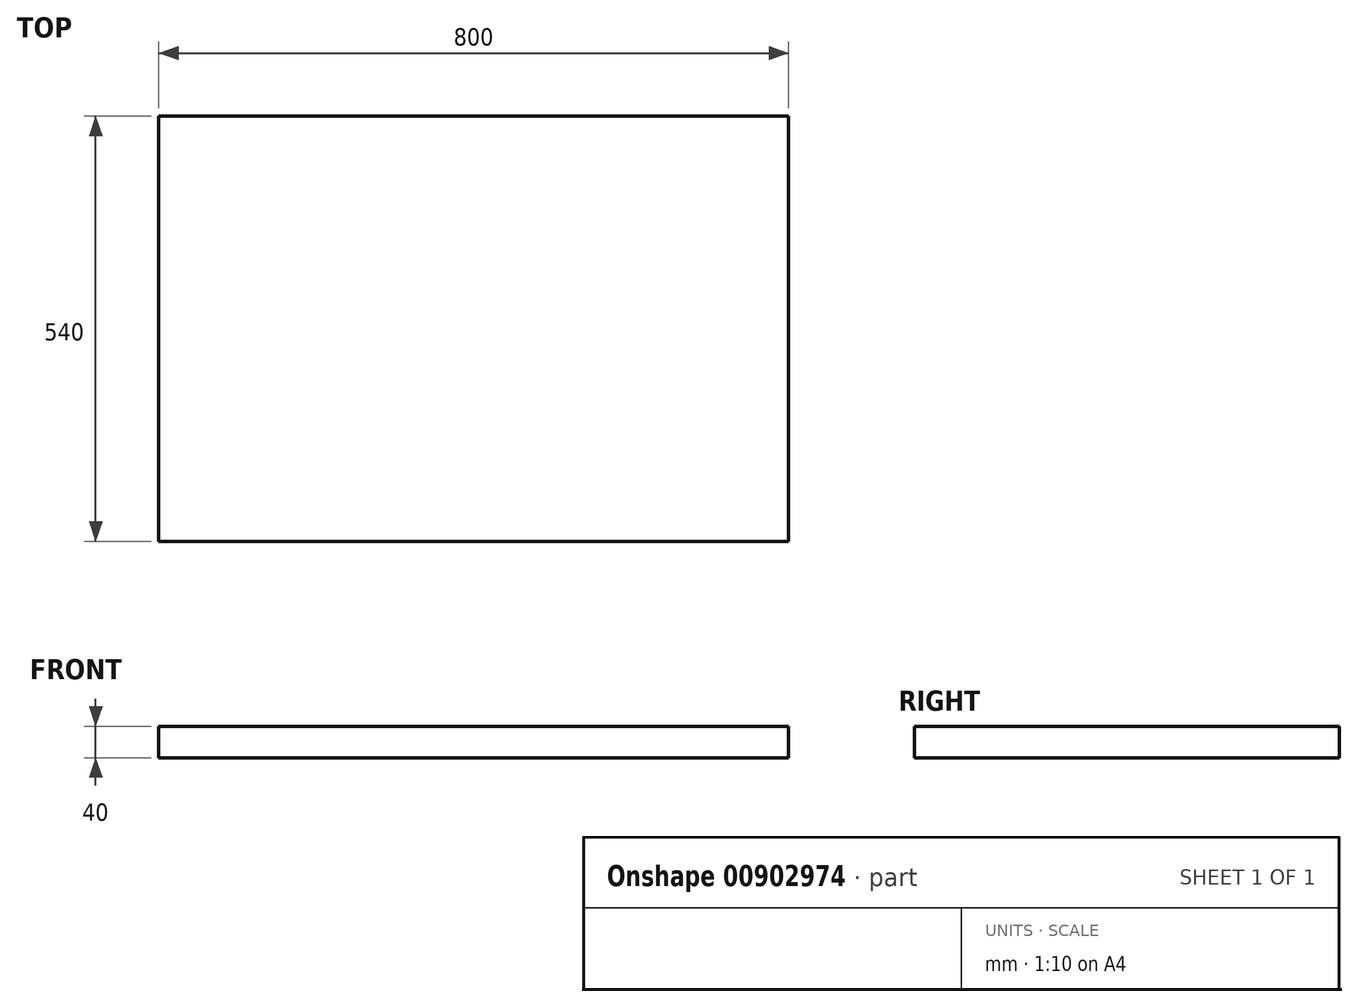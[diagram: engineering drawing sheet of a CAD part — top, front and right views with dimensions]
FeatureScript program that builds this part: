
annotation { "Feature Type Name" : "Feature", "Feature Type Description" : "" }
export const myFeature = defineFeature(function(context is Context, id is Id, definition is map)
    precondition{}
    {
        {
            var Q0;
            Q0=qCreatedBy(makeId("Top.planeOp"),FACE);
            var sketch = newSketch(context, id + "F0", { "sketchPlane" : qUnion([Q0])});
            skLineSegment(sketch, "E0.bottom", {"start": v(400, -270) * mm, "end": v(-400, -270) * mm});
            skLineSegment(sketch, "E0.top", {"start": v(400, 270) * mm, "end": v(-400, 270) * mm});
            skLineSegment(sketch, "E0.left", {"start": v(400, -270) * mm, "end": v(400, 270) * mm});
            skLineSegment(sketch, "E0.right", {"start": v(-400, -270) * mm, "end": v(-400, 270) * mm});
            skPoint(sketch, "E0.middle", {"position": v(0, 0) * mm});
            skSolve(sketch);
        }
        {
            var Q0;
            Q0=makeQuery(id+"F0.imprint","IMPRINT",FACE,{"disambiguationData":[TD([[makeQuery(id+"F0.imprint","IMPRINT",EDGE,{"derivedFrom":sQuery(id+"F0.wireOp",EDGE,"E0.bottom")}),-1.0]])]});
            extrude(context, id + "F1", {"entities" : qUnion([Q0]), "oppositeDirection" : true, "depth" : 40 * mm, "offsetDistance" : 25 * mm});
        }
    });
